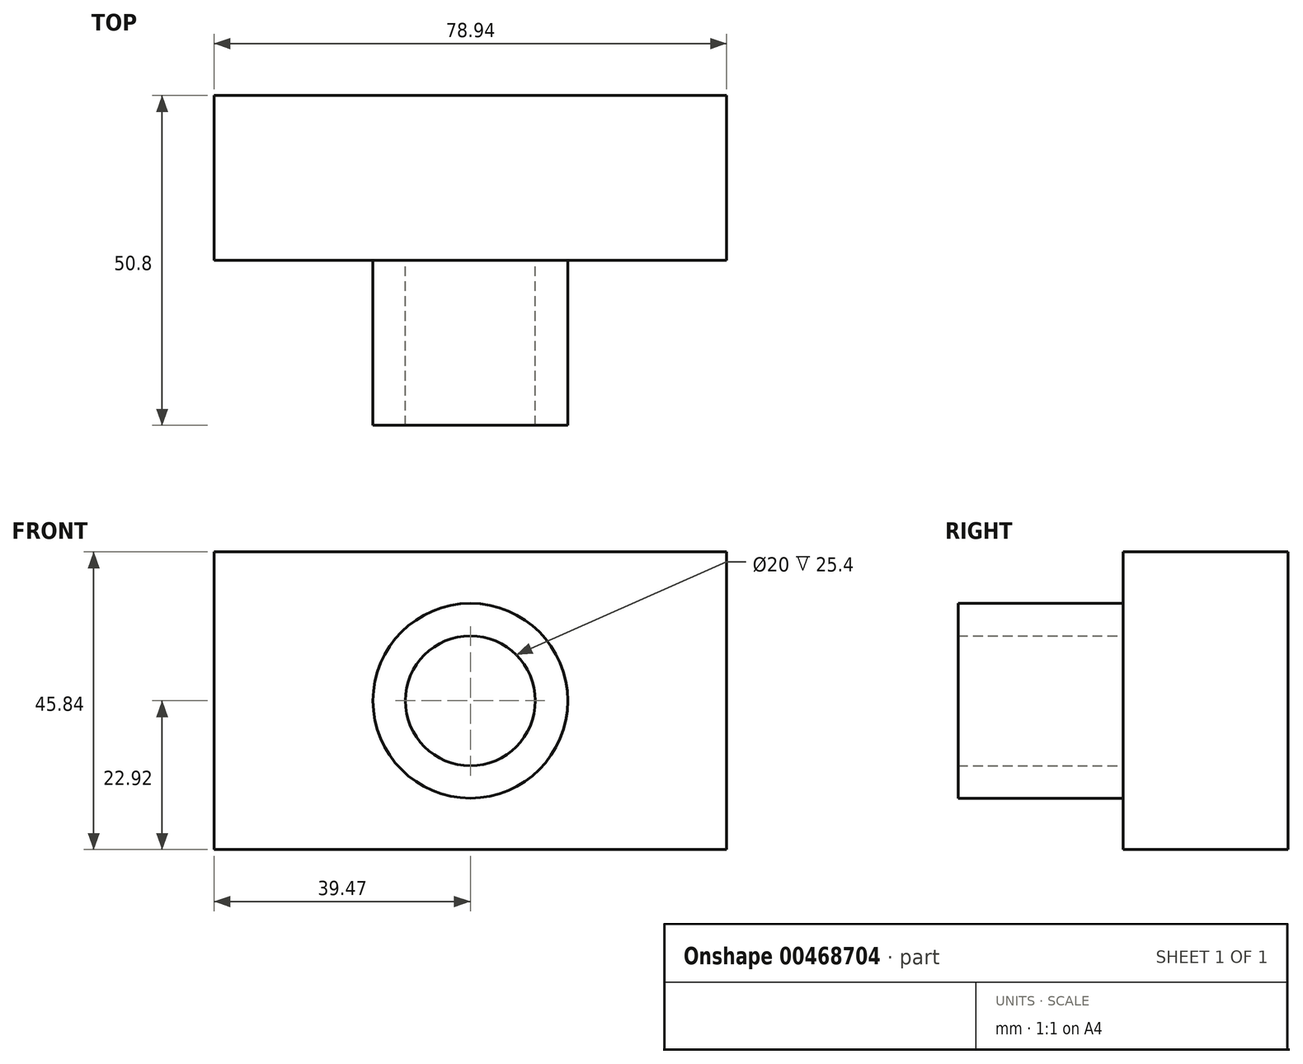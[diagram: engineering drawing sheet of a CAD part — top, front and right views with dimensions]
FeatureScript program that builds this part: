
annotation { "Feature Type Name" : "Feature", "Feature Type Description" : "" }
export const myFeature = defineFeature(function(context is Context, id is Id, definition is map)
    precondition{}
    {
        {
            var Q0;
            Q0=qCreatedBy(makeId("Front.planeOp"),FACE);
            var sketch = newSketch(context, id + "F0", { "sketchPlane" : qUnion([Q0])});
            skLineSegment(sketch, "E0.bottom", {"start": v(39.47, 22.92) * mm, "end": v(-39.47, 22.92) * mm});
            skLineSegment(sketch, "E0.top", {"start": v(39.47, -22.92) * mm, "end": v(-39.47, -22.92) * mm});
            skLineSegment(sketch, "E0.left", {"start": v(39.47, 22.92) * mm, "end": v(39.47, -22.92) * mm});
            skLineSegment(sketch, "E0.right", {"start": v(-39.47, 22.92) * mm, "end": v(-39.47, -22.92) * mm});
            skPoint(sketch, "E0.middle", {"position": v(0, 0) * mm});
            skSolve(sketch);
        }
        {
            var Q0;
            Q0=makeQuery(id+"F0.imprint","IMPRINT",FACE,{"disambiguationData":[TD([[makeQuery(id+"F0.imprint","IMPRINT",EDGE,{"derivedFrom":sQuery(id+"F0.wireOp",EDGE,"E0.bottom")}),1.0]])]});
            extrude(context, id + "F1", {"entities" : qUnion([Q0]), "endBound" : BoundingType.SYMMETRIC, "depth" : 25.4 * mm});
        }
        {
            var Q0;
            Q0=makeQuery(id+"F1.opExtrude","CAP_FACE",FACE,{"disambiguationData":[OSD([sQuery(id+"F0.wireOp",EDGE,"E0.bottom"),sQuery(id+"F0.wireOp",EDGE,"E0.top"),sQuery(id+"F0.wireOp",EDGE,"E0.left"),sQuery(id+"F0.wireOp",EDGE,"E0.right")])],"isStart":false});
            var sketch = newSketch(context, id + "F2", { "sketchPlane" : qUnion([Q0])});
            skCircle(sketch, "E1", {"center": v(0, 0) * mm, "radius": 10 * mm});
            skCircle(sketch, "E2", {"center": v(0, 0) * mm, "radius": 15 * mm});
            skSolve(sketch);
        }
        {
            var Q0;
            Q0=makeQuery(id+"F2.imprint","IMPRINT",FACE,{"disambiguationData":[TD([[makeQuery(id+"F2.imprint","IMPRINT",EDGE,{"derivedFrom":sQuery(id+"F2.wireOp",EDGE,"E1")}),-1.0]])]});
            extrude(context, id + "F3", {"entities" : qUnion([Q0]), "operationType" : NewBodyOperationType.ADD, "depth" : 25.4 * mm});
        }
    });
